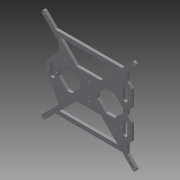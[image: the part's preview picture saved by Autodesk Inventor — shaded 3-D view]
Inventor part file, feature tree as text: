
AUTODESK INVENTOR PART (.ipt)
format: ipt  version: 2015 (Build 190159000, 159)  size: 692,224 bytes
history: native  units: mm
features: extrude x1, sketch x1
ambient origin geometry x8: Origin, YZ Plane, XZ Plane, XY Plane, X Axis, Y Axis, Z Axis, Center Point
bodies: Solid1 (feature_tree)
feature tree (2):
  extrude  "Extrusion1"  [1 undecoded]
  sketch  "Sketch1"  dims[d0=6.0mm d1=0.0mm]
note: 1 required parameter value undecoded (feature->parameter linkage not recoverable at this tier; creation-order binding heuristic only, values carry confidence <= 0.55)
